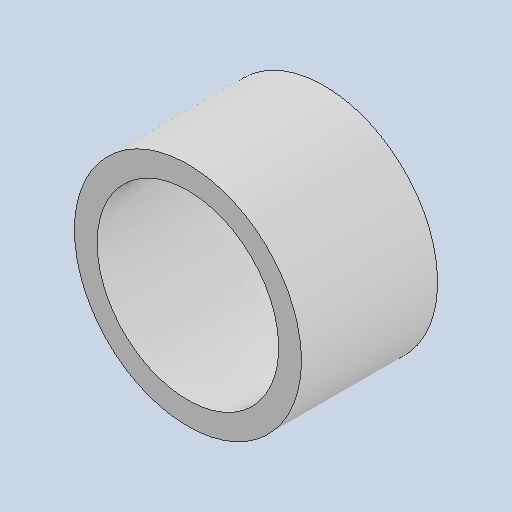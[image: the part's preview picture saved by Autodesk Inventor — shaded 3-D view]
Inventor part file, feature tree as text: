
AUTODESK INVENTOR PART (.ipt)
format: ipt  version: 2023 (Build 270158030, 158C)  size: 105,984 bytes
history: native  units: in
note: dims shown in document units (in); Inventor stores cm internally (conversion verified against a paired STEP export)
features: extrude x1
ambient origin geometry x8: Origin, YZ Plane, XZ Plane, XY Plane, X Axis, Y Axis, Z Axis, Center Point
bodies: Solid1 (feature_tree)
feature tree (1):
  extrude  "Extrude1"  [1 undecoded]
note: 1 required parameter value undecoded (feature->parameter linkage not recoverable at this tier; creation-order binding heuristic only, values carry confidence <= 0.55)
